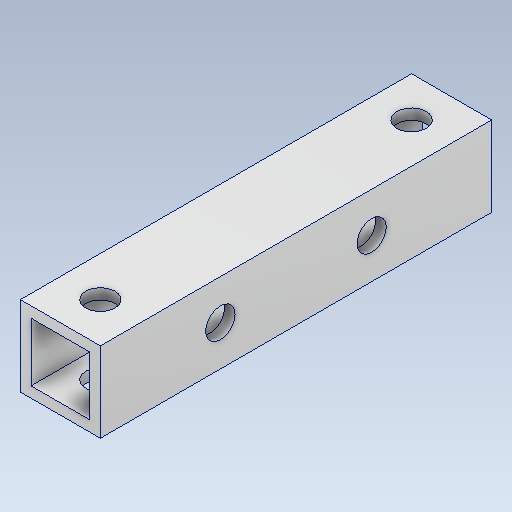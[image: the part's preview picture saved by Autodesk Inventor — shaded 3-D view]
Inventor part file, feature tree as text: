
AUTODESK INVENTOR PART (.ipt)
format: ipt  version: 2020.3 (Build 243373000, 373)  size: 140,800 bytes
history: native  units: mm
features: sketch x3, hole x2, other x1, extrude x1
ambient origin geometry x8: Origin, YZ Plane, XZ Plane, XY Plane, X Axis, Y Axis, Z Axis, Center Point
bodies: Body1 (feature_tree)
feature tree (7):
  other  "ソリッド1"
  extrude  "押し出し1"  Depth=9.0mm
  hole  "穴1"  [1 undecoded]
  hole  "穴2"  [1 undecoded]
  sketch  "スケッチ1"
  sketch  "スケッチ2"
  sketch  "スケッチ3"
note: 2 required parameter values undecoded (feature->parameter linkage not recoverable at this tier; creation-order binding heuristic only, values carry confidence <= 0.55)
